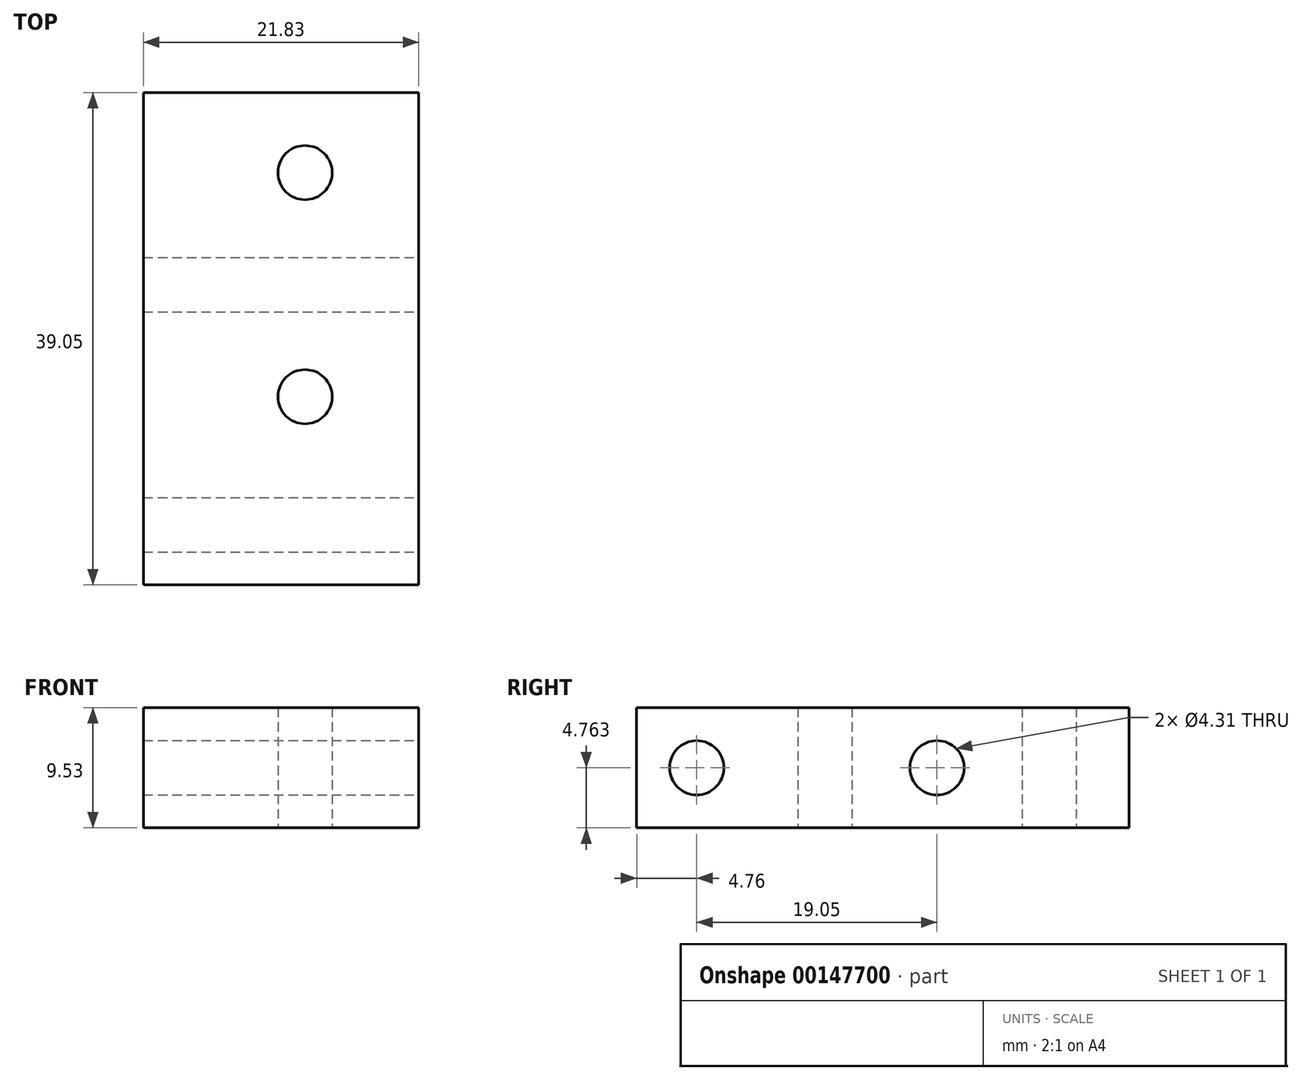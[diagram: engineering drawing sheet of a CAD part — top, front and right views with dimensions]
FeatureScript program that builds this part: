
annotation { "Feature Type Name" : "Feature", "Feature Type Description" : "" }
export const myFeature = defineFeature(function(context is Context, id is Id, definition is map)
    precondition{}
    {
        {
            var Q0;
            Q0=qCreatedBy(makeId("Top.planeOp"),FACE);
            var sketch = newSketch(context, id + "F0", { "sketchPlane" : qUnion([Q0])});
            skLineSegment(sketch, "E0.bottom", {"start": v(0, 0) * mm, "end": v(21.83, 0) * mm});
            skLineSegment(sketch, "E0.top", {"start": v(0, -39.05) * mm, "end": v(21.83, -39.05) * mm});
            skLineSegment(sketch, "E0.left", {"start": v(0, 0) * mm, "end": v(0, -39.05) * mm});
            skLineSegment(sketch, "E0.right", {"start": v(21.83, 0) * mm, "end": v(21.83, -39.05) * mm});
            skLineSegment(sketch, "E1", {"start": v(12.81, 0) * mm, "end": v(12.81, -6.35) * mm, "construction": true});
            skLineSegment(sketch, "E2", {"start": v(12.81, -6.35) * mm, "end": v(12.81, -24.13) * mm, "construction": true});
            skCircle(sketch, "E3", {"center": v(12.81, -6.35) * mm, "radius": 2.15 * mm});
            skCircle(sketch, "E4", {"center": v(12.81, -24.13) * mm, "radius": 2.15 * mm});
            skLineSegment(sketch, "E5", {"start": v(12.81, -24.13) * mm, "end": v(12.81, -39.05) * mm, "construction": true});
            skPoint(sketch, "E6", {"position": v(12.81, -15.24) * mm});
            skSolve(sketch);
        }
        {
            var Q0;
            Q0=qSketchRegion(id+"F0",true);
            extrude(context, id + "F1", {"entities" : qUnion([Q0]), "depth" : 9.52 * mm});
        }
        {
            var Q0;
            Q0=makeQuery(id+"F1.opExtrude","SWEPT_FACE",FACE,{"disambiguationData":[OSD([sQuery(id+"F0.wireOp",EDGE,"E0.right")])]});
            var sketch = newSketch(context, id + "F2", { "sketchPlane" : qUnion([Q0])});
            skLineSegment(sketch, "E7", {"start": v(-39.05, 4.76) * mm, "end": v(-34.3, 4.76) * mm, "construction": true});
            skLineSegment(sketch, "E8", {"start": v(-6.35, 4.76) * mm, "end": v(-24.13, 4.76) * mm, "construction": true});
            skLineSegment(sketch, "E9", {"start": v(-6.35, 4.76) * mm, "end": v(-6.35, 9.53) * mm, "construction": true});
            skLineSegment(sketch, "E10", {"start": v(-24.13, 4.76) * mm, "end": v(-24.13, 9.53) * mm, "construction": true});
            skCircle(sketch, "E11", {"center": v(-34.3, 4.76) * mm, "radius": 2.15 * mm});
            skCircle(sketch, "E12", {"center": v(-15.24, 4.76) * mm, "radius": 2.15 * mm});
            skSolve(sketch);
        }
        {
            var Q0;
            Q0=qSketchRegion(id+"F2",true);
            var Q1;
            Q1=makeQuery(id+"F1.opExtrude","SWEPT_FACE",FACE,{"disambiguationData":[OSD([sQuery(id+"F0.wireOp",EDGE,"E0.left")])]});
            extrude(context, id + "F3", {"entities" : qUnion([Q0]), "operationType" : NewBodyOperationType.REMOVE, "endBound" : BoundingType.UP_TO_SURFACE, "oppositeDirection" : true, "endBoundEntityFace" : qUnion([Q1]), "depth" : 25.4 * mm});
        }
    });
